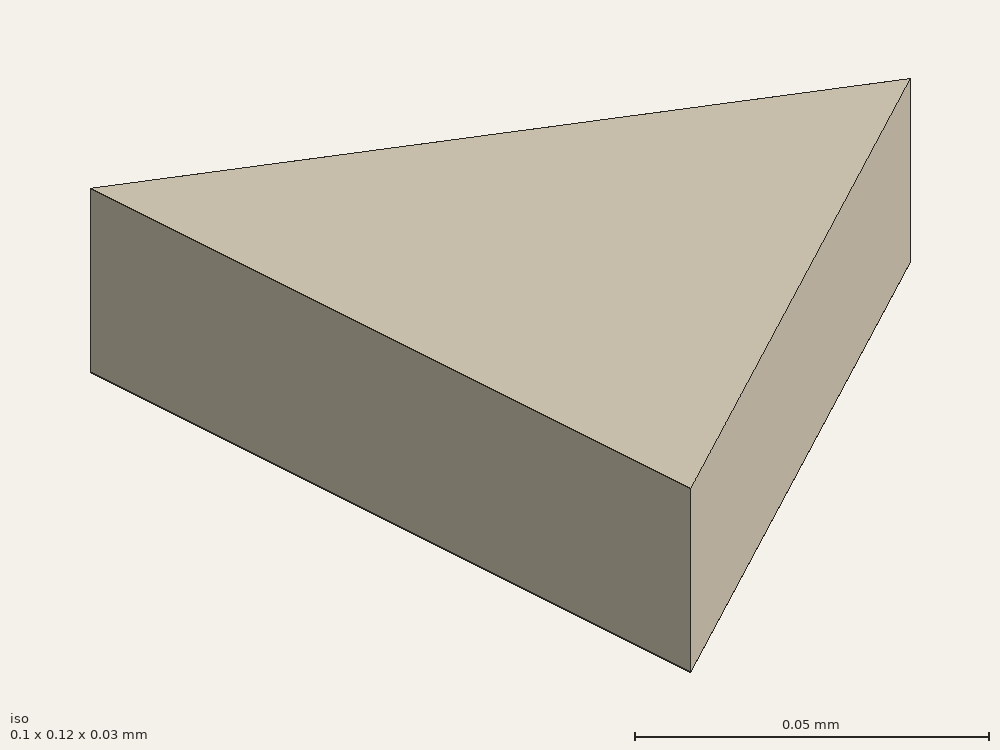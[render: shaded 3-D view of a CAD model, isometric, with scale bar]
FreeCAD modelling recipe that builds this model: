
FCSTD DOCUMENT  (FreeCAD 0.15R4671 (Git))
Label: triangle0
License: All rights reserved
LicenseURL: http://en.wikipedia.org/wiki/All_rights_reserved
objects: Sketcher::SketchObject×1, PartDesign::Pad×1
note: 3 computed .brp shape members not serialized (recipe doc carries the construction recipe); baked Part::Feature solids carry a one-line shape summary decoded from their .brp

FEATURE [Sketcher::SketchObject] Sketch
  sketch-geometry (3):
    g0: LineSegment StartX=-0.03464 StartY=0.06 StartZ=0 EndX=-0.03464 EndY=-0.06 EndZ=0
    g1: LineSegment StartX=-0.03464 StartY=-0.06 StartZ=0 EndX=0.069283 EndY=0 EndZ=0
    g2: LineSegment StartX=0.069283 StartY=0 StartZ=0 EndX=-0.03464 EndY=0.06 EndZ=0
  constraints (9):
    c: Coincident(g0,g1)
    c: Coincident(g1,g2)
    c: Coincident(g0,g2)
    c: Equal(g2,g1)
    c: Equal(g1,g0)
    c: Distance(g2) = 0.12
    c: Vertical(g0)
    c: Distance(g-1,g0) = 0.03464
    c: DistanceY(g-1,g1) = 0
FEATURE [PartDesign::Pad] Pad
  Length = 0.03
  Length2 = 100
  Midplane = true
  Sketch = -> Sketch
  Type = 0
